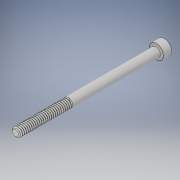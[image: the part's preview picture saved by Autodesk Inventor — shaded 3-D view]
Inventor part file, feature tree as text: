
AUTODESK INVENTOR PART (.ipt)
format: ipt  version: 2018 (Build 220112000, 112)  size: 781,824 bytes
history: native  units: in
note: dims shown in document units (in); Inventor stores cm internally (conversion verified against a paired STEP export)
features: chamfer x1
ambient origin geometry x8: Origin, YZ Plane, XZ Plane, XY Plane, X Axis, Y Axis, Z Axis, Center Point
bodies: Solid1 (feature_tree)
feature tree (1):
  chamfer  "Chamfer2"  [1 undecoded]
note: 1 required parameter value undecoded (feature->parameter linkage not recoverable at this tier; creation-order binding heuristic only, values carry confidence <= 0.55)
